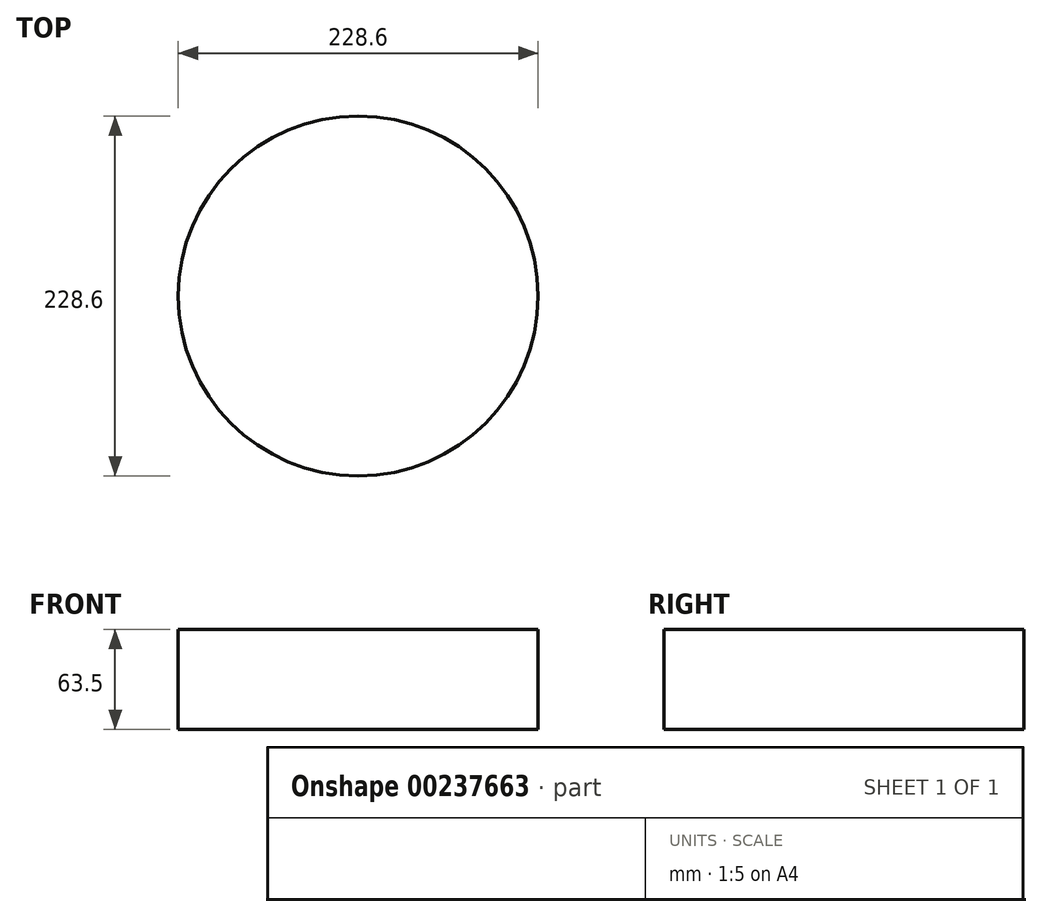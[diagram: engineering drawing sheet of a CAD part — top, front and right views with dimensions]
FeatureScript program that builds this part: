
annotation { "Feature Type Name" : "Feature", "Feature Type Description" : "" }
export const myFeature = defineFeature(function(context is Context, id is Id, definition is map)
    precondition{}
    {
        {
            var Q0;
            Q0=qCreatedBy(makeId("Top.planeOp"),FACE);
            var sketch = newSketch(context, id + "F0", { "sketchPlane" : qUnion([Q0])});
            skCircle(sketch, "E0", {"center": v(0, 0) * mm, "radius": 114.3 * mm});
            skSolve(sketch);
        }
        {
            var Q0;
            Q0=makeQuery(id+"F0.imprint","IMPRINT",FACE,{"disambiguationData":[TD([[makeQuery(id+"F0.imprint","IMPRINT",EDGE,{"derivedFrom":sQuery(id+"F0.wireOp",EDGE,"E0")}),1.0]])]});
            extrude(context, id + "F1", {"entities" : qUnion([Q0]), "depth" : 63.5 * mm});
        }
    });
